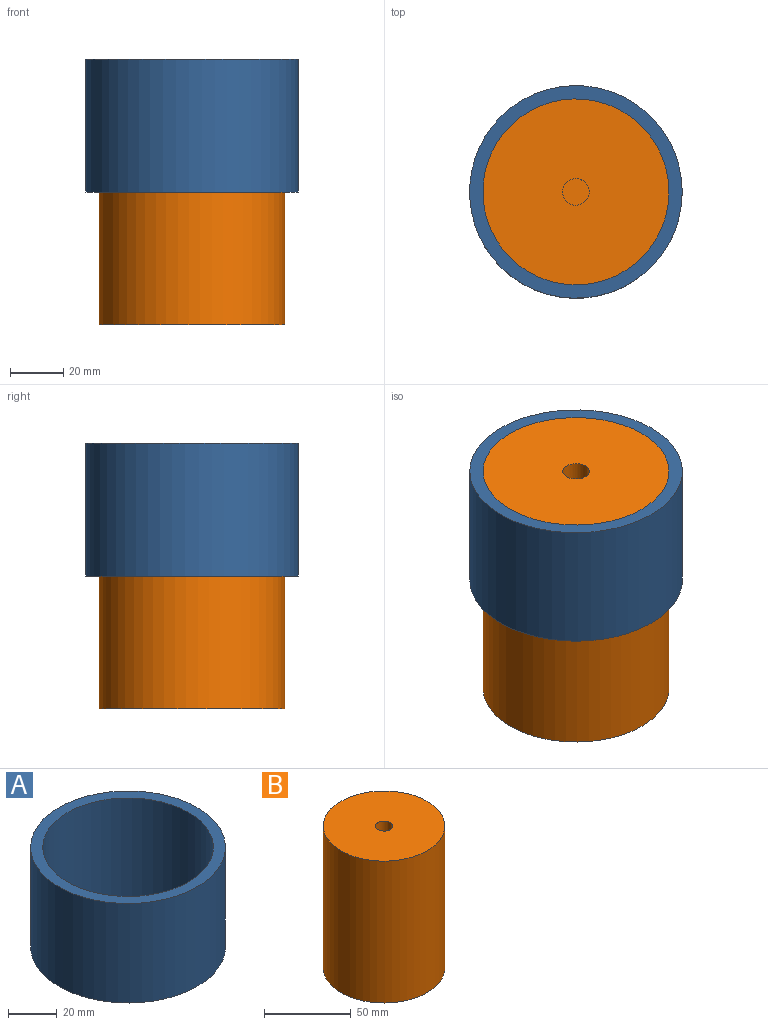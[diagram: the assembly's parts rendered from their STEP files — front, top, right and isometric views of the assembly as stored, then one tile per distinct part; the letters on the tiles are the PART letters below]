
ASSEMBLY  parts=2 mates=1
PART A: 4 faces, bbox 80x80x50 mm
  f0: cylinder r=35mm len=70mm, axis (0,0,-1), area 10995.6mm2, adj f2,f3
  f1: cylinder r=40mm len=80mm, axis (0,0,-1), area 12566.4mm2, adj f2,f3
  f2: plane 80x80mm, normal (0,0,1), area 1178.1mm2, adj f0,f1
  f3: plane 80x80mm, normal (0,0,-1), area 1178.1mm2, adj f0,f1
PART B: 5 faces, bbox 70x70x100 mm
  f0: cylinder r=35mm len=100mm, axis (0,0,-1), area 21991.1mm2, adj f1,f2
  f1: plane 70x70mm, normal (0,0,1), area 3769.9mm2, adj f0,f3
  f2: plane 70x70mm, normal (0,0,-1), area 3848.5mm2, adj f0
  f3: cylinder r=5mm len=10mm, axis (0,0,1), area 314.2mm2, adj f1,f4
  f4: plane 10x10mm, normal (0,0,1), area 78.5mm2, adj f3
PLACE A t=(10.41,21.74,51.81)mm
PLACE B t=(10.41,21.74,1.81)mm
MATE slider A.f0 <-> B.f0  axis (0,0,1) through (10.41,21.74,101.81)mm
